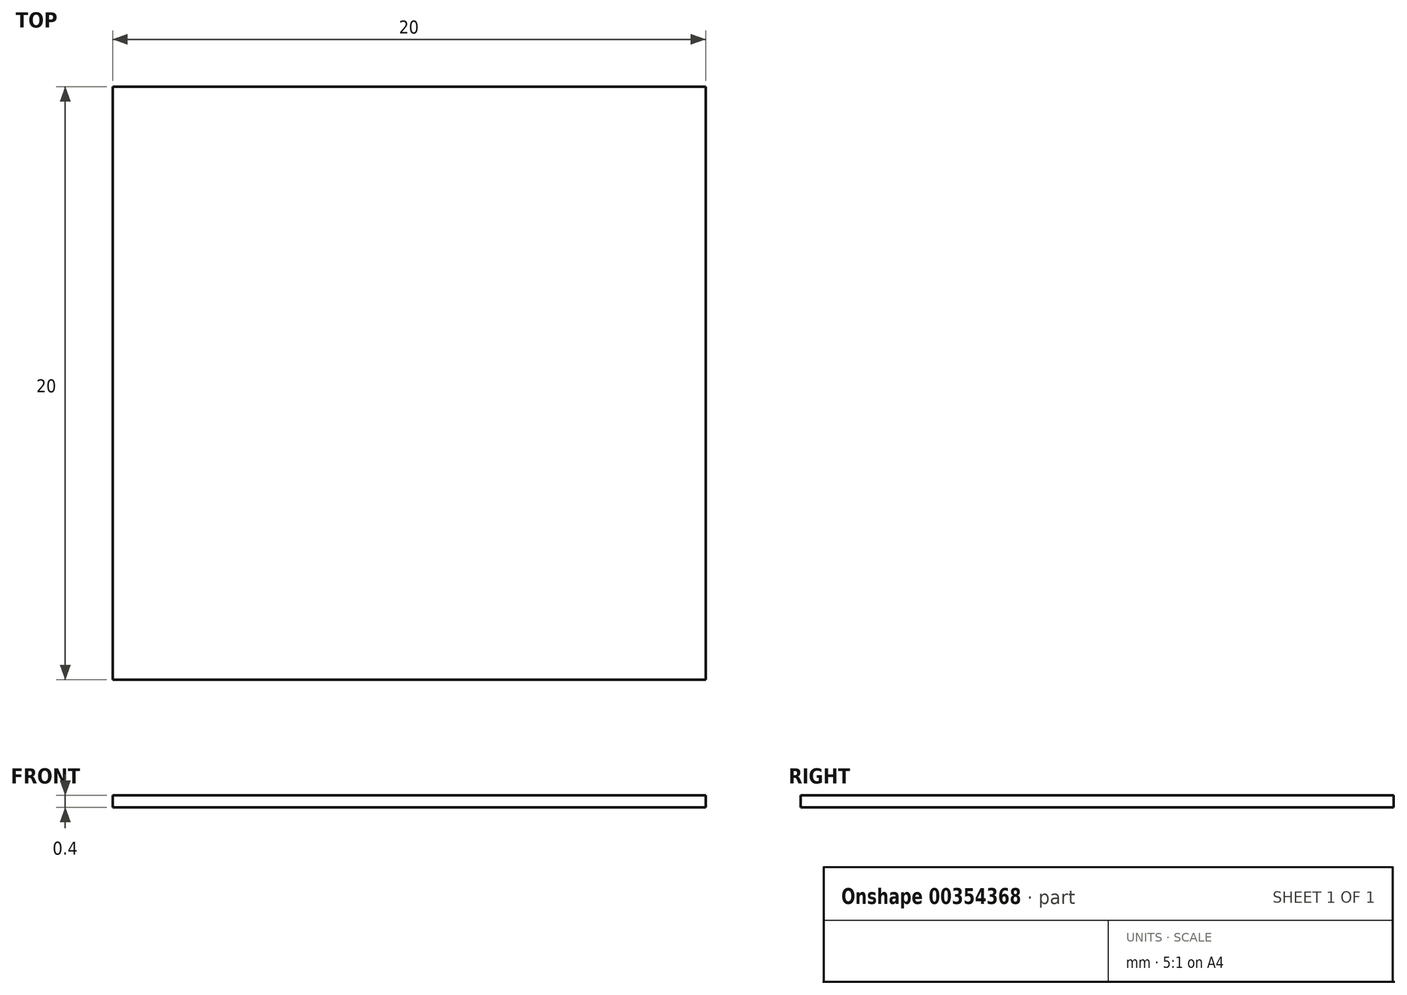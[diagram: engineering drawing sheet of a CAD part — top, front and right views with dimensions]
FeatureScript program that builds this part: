
annotation { "Feature Type Name" : "Feature", "Feature Type Description" : "" }
export const myFeature = defineFeature(function(context is Context, id is Id, definition is map)
    precondition{}
    {
        {
            var Q0;
            Q0=qCreatedBy(makeId("Top.planeOp"),FACE);
            var sketch = newSketch(context, id + "F0", { "sketchPlane" : qUnion([Q0])});
            skLineSegment(sketch, "E0.bottom", {"start": v(10, 10) * mm, "end": v(-10, 10) * mm});
            skLineSegment(sketch, "E0.top", {"start": v(10, -10) * mm, "end": v(-10, -10) * mm});
            skLineSegment(sketch, "E0.left", {"start": v(10, 10) * mm, "end": v(10, -10) * mm});
            skLineSegment(sketch, "E0.right", {"start": v(-10, 10) * mm, "end": v(-10, -10) * mm});
            skPoint(sketch, "E0.middle", {"position": v(0, 0) * mm});
            skSolve(sketch);
        }
        {
            var Q0;
            Q0=makeQuery(id+"F0.imprint","IMPRINT",FACE,{"disambiguationData":[TD([[makeQuery(id+"F0.imprint","IMPRINT",EDGE,{"derivedFrom":sQuery(id+"F0.wireOp",EDGE,"E0.bottom")}),1.0]])]});
            extrude(context, id + "F1", {"entities" : qUnion([Q0]), "depth" : 0.4 * mm});
        }
    });
